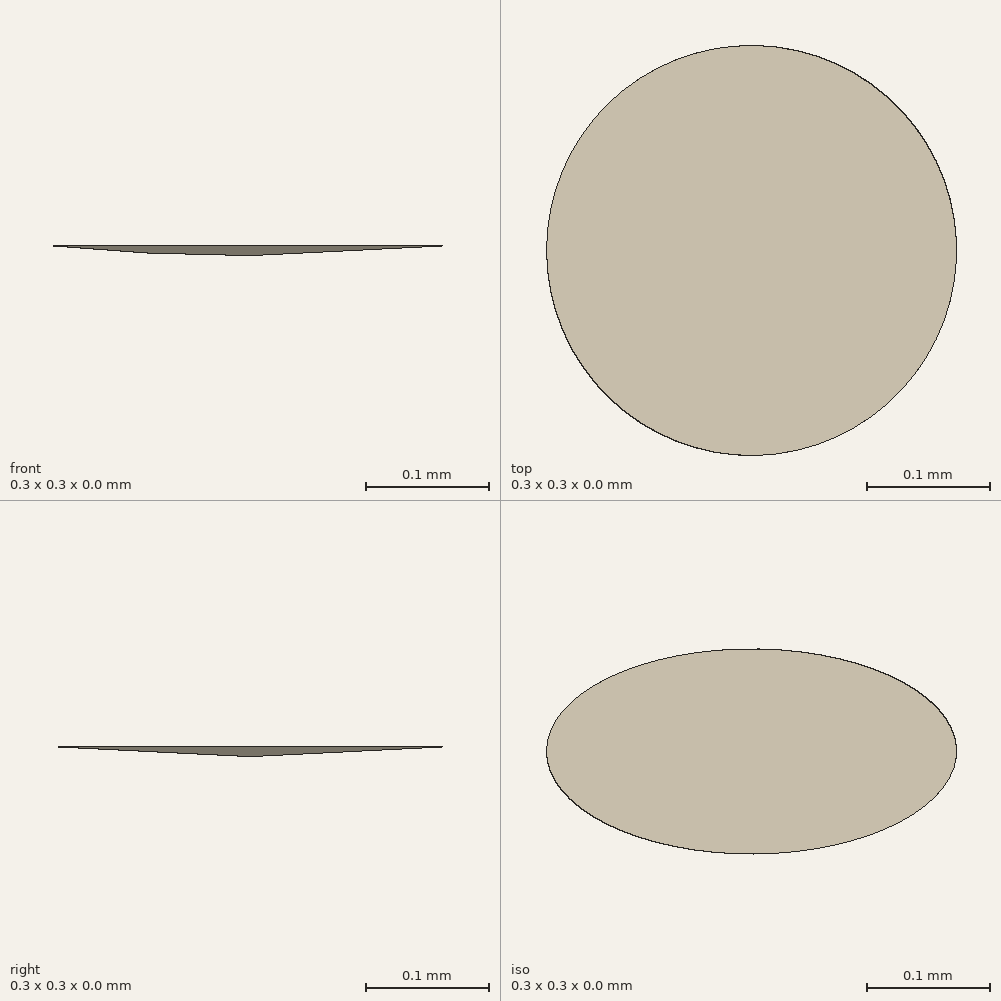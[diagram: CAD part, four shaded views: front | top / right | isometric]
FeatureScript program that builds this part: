
annotation { "Feature Type Name" : "Feature", "Feature Type Description" : "" }
export const myFeature = defineFeature(function(context is Context, id is Id, definition is map)
    precondition{}
    {
        {
            var Q0;
            Q0=qCreatedBy(makeId("Front.planeOp"),FACE);
            var sketch = newSketch(context, id + "F0", { "sketchPlane" : qUnion([Q0])});
            skLineSegment(sketch, "E0", {"start": v(0, 0) * mm, "end": v(0, 2412.07) * mm});
            skLineSegment(sketch, "E1", {"start": v(-0.85, 1869.08) * mm, "end": v(-0.85, 0.34) * mm});
            skArc(sketch, "E2", {"start": v(-0.75, 0.18) * mm, "mid": v(-0.39, 0.04) * mm, "end": v(0, 0) * mm});
            skArc(sketch, "E3", {"start": v(-0.85, 0.34) * mm, "mid": v(-0.82, 0.24) * mm, "end": v(-0.75, 0.18) * mm});
            skLineSegment(sketch, "E4", {"start": v(-0.85, 0.34) * mm, "end": v(-0.85, 0) * mm});
            skLineSegment(sketch, "E5", {"start": v(-0.85, 0) * mm, "end": v(0, 0) * mm});
            skSolve(sketch);
        }
        {
            var Q0;
            {var subQ0=sQuery(id+"F0.wireOp",EDGE,"E2");Q0=makeQuery(id+"F0.imprint","IMPRINT",FACE,{"disambiguationData":[TD([[makeQuery(id+"F0.imprint","IMPRINT",EDGE,{"derivedFrom":subQ0}),1.0]])]});}
            var Q1;
            Q1=sQuery(id+"F0.wireOp",EDGE,"E0");
            revolve(context, id + "F1", {"surfaceOperationType" : NewSurfaceOperationType.NEW, "entities" : qUnion([Q0]), "axis" : qUnion([Q1]), "revolveType" : RevolveType.FULL});
        }
    });
